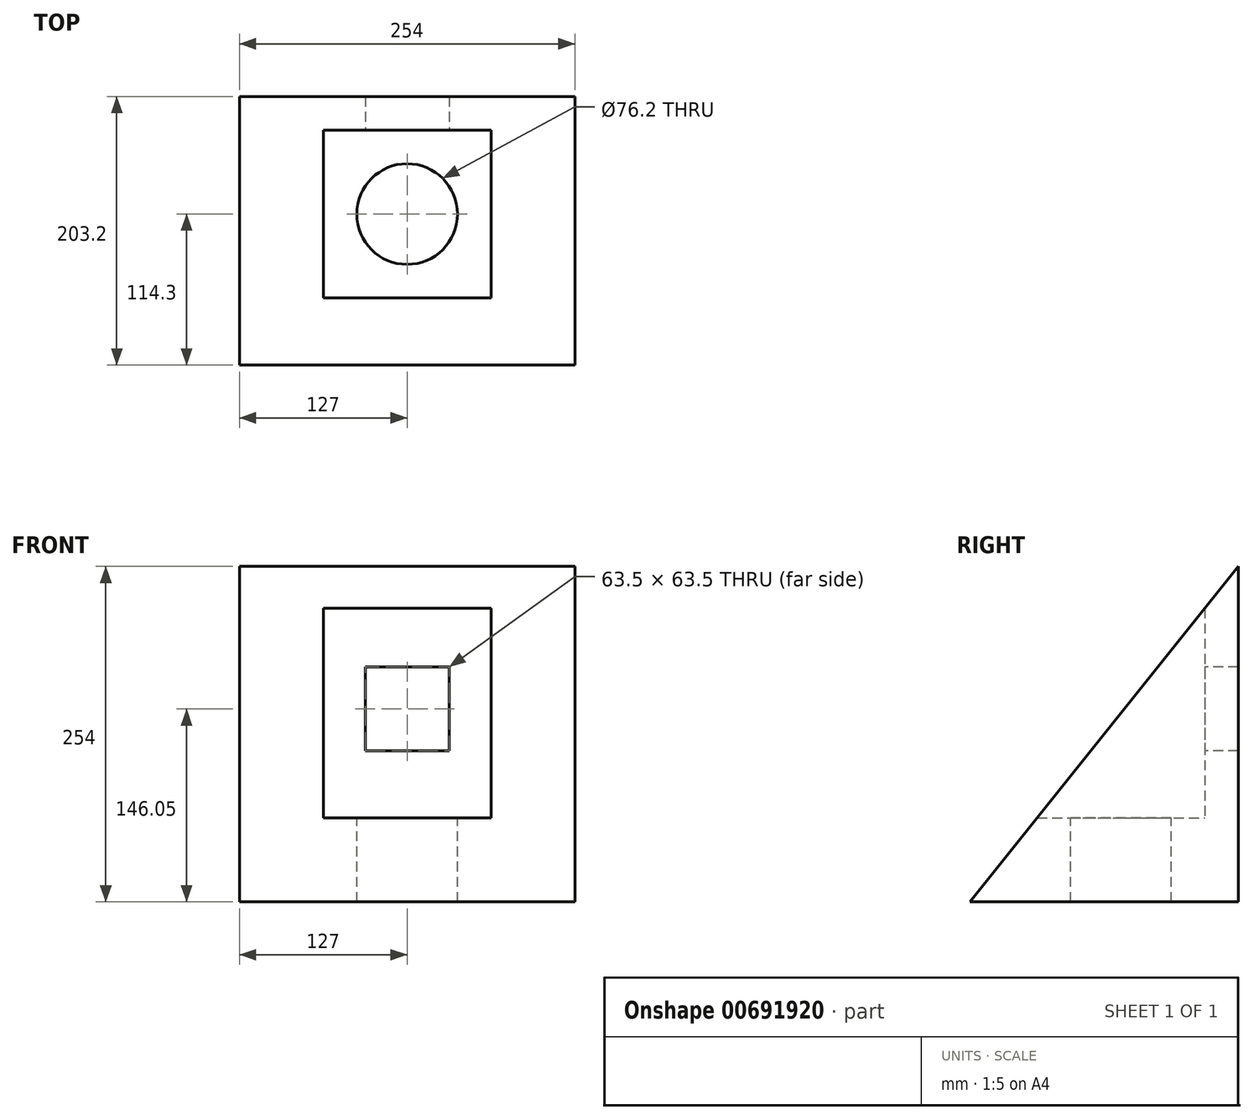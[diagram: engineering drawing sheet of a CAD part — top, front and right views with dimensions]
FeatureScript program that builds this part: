
annotation { "Feature Type Name" : "Feature", "Feature Type Description" : "" }
export const myFeature = defineFeature(function(context is Context, id is Id, definition is map)
    precondition{}
    {
        {
            var Q0;
            Q0=qCreatedBy(makeId("Front.planeOp"),FACE);
            var sketch = newSketch(context, id + "F0", { "sketchPlane" : qUnion([Q0])});
            skLineSegment(sketch, "E0.bottom", {"start": v(-127, -127) * mm, "end": v(127, -127) * mm});
            skLineSegment(sketch, "E0.top", {"start": v(-127, 127) * mm, "end": v(127, 127) * mm});
            skLineSegment(sketch, "E0.left", {"start": v(-127, -127) * mm, "end": v(-127, 127) * mm});
            skLineSegment(sketch, "E0.right", {"start": v(127, -127) * mm, "end": v(127, 127) * mm});
            skPoint(sketch, "E0.middle", {"position": v(0, 0) * mm});
            skLineSegment(sketch, "E1.0", {"start": v(-63.5, 88.9) * mm, "end": v(63.5, 88.9) * mm});
            skLineSegment(sketch, "E2.0", {"start": v(-63.5, -63.5) * mm, "end": v(63.5, -63.5) * mm});
            skLineSegment(sketch, "E3.0", {"start": v(63.5, -63.5) * mm, "end": v(63.5, 88.9) * mm});
            skLineSegment(sketch, "E4.0", {"start": v(-63.5, -63.5) * mm, "end": v(-63.5, 88.9) * mm});
            skLineSegment(sketch, "E5.0", {"start": v(-31.75, 50.8) * mm, "end": v(31.75, 50.8) * mm});
            skLineSegment(sketch, "E6.0", {"start": v(-31.75, -12.7) * mm, "end": v(31.75, -12.7) * mm});
            skLineSegment(sketch, "E7.0", {"start": v(31.75, -12.7) * mm, "end": v(31.75, 50.8) * mm});
            skLineSegment(sketch, "E8.0", {"start": v(-31.75, -12.7) * mm, "end": v(-31.75, 50.8) * mm});
            skSolve(sketch);
        }
        {
            var Q0;
            Q0=qCreatedBy(makeId("Top.planeOp"),FACE);
            var sketch = newSketch(context, id + "F1", { "sketchPlane" : qUnion([Q0])});
            skLineSegment(sketch, "E9.bottom", {"start": v(-127, -101.6) * mm, "end": v(127, -101.6) * mm});
            skLineSegment(sketch, "E9.top", {"start": v(-127, 101.6) * mm, "end": v(127, 101.6) * mm});
            skLineSegment(sketch, "E9.left", {"start": v(-127, -101.6) * mm, "end": v(-127, 101.6) * mm});
            skLineSegment(sketch, "E9.right", {"start": v(127, -101.6) * mm, "end": v(127, 101.6) * mm});
            skPoint(sketch, "E9.middle", {"position": v(0, 0) * mm});
            skLineSegment(sketch, "E10.0", {"start": v(-63.5, 76.2) * mm, "end": v(63.5, 76.2) * mm});
            skLineSegment(sketch, "E11.0", {"start": v(63.5, -50.8) * mm, "end": v(63.5, 76.2) * mm});
            skLineSegment(sketch, "E12.0", {"start": v(-63.5, -50.8) * mm, "end": v(-63.5, 76.2) * mm});
            skLineSegment(sketch, "E13.0", {"start": v(-63.5, -50.8) * mm, "end": v(63.5, -50.8) * mm});
            skCircle(sketch, "E14", {"center": v(0, 12.7) * mm, "radius": 38.1 * mm});
            skSolve(sketch);
        }
        {
            var Q0;
            Q0=qCreatedBy(makeId("Right.planeOp"),FACE);
            var sketch = newSketch(context, id + "F2", { "sketchPlane" : qUnion([Q0])});
            skLineSegment(sketch, "E15.bottom", {"start": v(101.6, -127) * mm, "end": v(-101.6, -127) * mm});
            skLineSegment(sketch, "E15.left", {"start": v(101.6, -127) * mm, "end": v(101.6, 127) * mm});
            skPoint(sketch, "E15.middle", {"position": v(0, 0) * mm});
            skPoint(sketch, "E15.right.end.orphan", {"position": v(-101.6, 127) * mm});
            skLineSegment(sketch, "E16", {"start": v(101.6, 127) * mm, "end": v(-101.6, -127) * mm});
            skSolve(sketch);
        }
        {
            var Q0;
            Q0=makeQuery(id+"F2.imprint","IMPRINT",FACE,{"disambiguationData":[TD([[makeQuery(id+"F2.imprint","IMPRINT",EDGE,{"derivedFrom":sQuery(id+"F2.wireOp",EDGE,"E15.bottom")}),-1.0]])]});
            extrude(context, id + "F3", {"entities" : qUnion([Q0]), "endBound" : BoundingType.SYMMETRIC, "depth" : 254 * mm, "offsetDistance" : 25.4 * mm});
        }
        {
            var Q0;
            Q0=makeQuery(id+"F1.imprint","IMPRINT",FACE,{"disambiguationData":[TD([[makeQuery(id+"F1.imprint","IMPRINT",EDGE,{"derivedFrom":sQuery(id+"F1.wireOp",EDGE,"E10.0")}),-1.0]])]});
            extrude(context, id + "F4", {"entities" : qUnion([Q0]), "operationType" : NewBodyOperationType.REMOVE, "depth" : 194.82 * mm, "offsetDistance" : 25.4 * mm});
        }
        {
            var Q0;
            Q0=makeQuery(id+"F1.imprint","IMPRINT",FACE,{"disambiguationData":[TD([[makeQuery(id+"F1.imprint","IMPRINT",EDGE,{"derivedFrom":sQuery(id+"F1.wireOp",EDGE,"E10.0")}),-1.0]])]});
            extrude(context, id + "F5", {"entities" : qUnion([Q0]), "operationType" : NewBodyOperationType.REMOVE, "oppositeDirection" : true, "depth" : 63.5 * mm, "offsetDistance" : 25.4 * mm});
        }
        {
            var Q0;
            Q0=makeQuery(id+"F1.imprint","IMPRINT",FACE,{"disambiguationData":[TD([[makeQuery(id+"F1.imprint","IMPRINT",EDGE,{"derivedFrom":sQuery(id+"F1.wireOp",EDGE,"E14")}),1.0]])]});
            extrude(context, id + "F6", {"entities" : qUnion([Q0]), "operationType" : NewBodyOperationType.REMOVE, "oppositeDirection" : true, "depth" : 281.43 * mm, "offsetDistance" : 25.4 * mm});
        }
        {
            var Q0;
            Q0=makeQuery(id+"F1.imprint","IMPRINT",FACE,{"disambiguationData":[TD([[makeQuery(id+"F1.imprint","IMPRINT",EDGE,{"derivedFrom":sQuery(id+"F1.wireOp",EDGE,"E14")}),1.0]])]});
            extrude(context, id + "F7", {"entities" : qUnion([Q0]), "operationType" : NewBodyOperationType.REMOVE, "depth" : 672.6 * mm, "offsetDistance" : 25.4 * mm});
        }
        {
            var Q0;
            Q0=makeQuery(id+"F0.imprint","IMPRINT",FACE,{"disambiguationData":[TD([[makeQuery(id+"F0.imprint","IMPRINT",EDGE,{"derivedFrom":sQuery(id+"F0.wireOp",EDGE,"E5.0")}),-1.0]])]});
            extrude(context, id + "F8", {"entities" : qUnion([Q0]), "operationType" : NewBodyOperationType.REMOVE, "oppositeDirection" : true, "depth" : 261.87 * mm, "offsetDistance" : 25.4 * mm});
        }
    });
